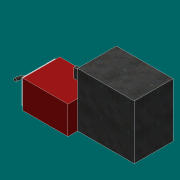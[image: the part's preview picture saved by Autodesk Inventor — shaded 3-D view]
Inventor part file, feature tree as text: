
AUTODESK INVENTOR PART (.ipt)
format: ipt  version: 2017 (Build 210142000, 142)  size: 147,456 bytes
history: native  units: in
note: dims shown in document units (in); Inventor stores cm internally (conversion verified against a paired STEP export)
features: sketch x6, extrude x4, plane x2, sweep x1, split x1, projected_geometry x1
ambient origin geometry x8: Origin, YZ Plane, XZ Plane, XY Plane, X Axis, Y Axis, Z Axis, Center Point
bodies: Solid1 (feature_tree)
feature tree (15):
  extrude  "Extrusion1"  Depth=9.5in
  extrude  "Extrusion2"  Depth=0.5in
  plane  "Work Plane1"
  sweep  "Sweep1"
  extrude  "Extrusion3"  Depth=0.75in
  extrude  "Extrusion4"  Depth=26.25in
  plane  "Work Plane2"
  split  "Split1"
  sketch  "Sketch1"  dims[d0=7.25in d1=9.5in]
  sketch  "Sketch2"  dims[d2=11.625in d3=0.0in d4=0.5in]
  projected_geometry  "Projected Loop1"
  sketch  "Sketch3"  dims[d5=0.75in d6=0.0in d7=4.125in]
  sketch  "Sketch4"  dims[d8=0.75in d9=0.75in]
  sketch  "Sketch5"  dims[d10=0.0in d11=0.0in d12=26.25in]
  sketch  "Sketch6"  dims[d13=3.0in d14=10.0in d15=14.0in d16=0.0in d17=5.0in d18=0.75in d19=2.25in d20=9.75in d21=0.0in d22=3.0in d23=0.0in]
